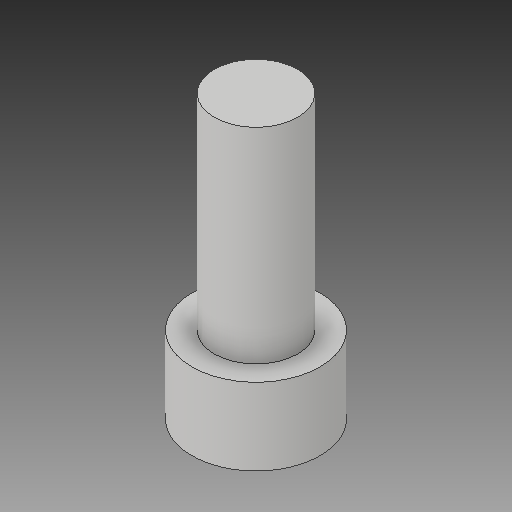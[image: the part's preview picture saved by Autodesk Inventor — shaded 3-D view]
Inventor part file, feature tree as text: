
AUTODESK INVENTOR PART (.ipt)
format: ipt  version: 2019 (Build 230136000, 136)  size: 97,792 bytes
history: native  units: mm
features: extrude x2, sketch x2
ambient origin geometry x8: Origin, YZ Plane, XZ Plane, XY Plane, X Axis, Y Axis, Z Axis, Center Point
bodies: Solid1 (feature_tree)
feature tree (4):
  extrude  "Extrusion1"  Depth=6.0mm TaperAngle=0.0deg
  extrude  "Extrusion2"  Depth=16.0mm TaperAngle=0.0deg
  sketch  "Sketch1"  dims[d0=10.0mm d1=6.0mm d2=0.0mm]
  sketch  "Sketch2"  dims[d3=6.5mm d4=16.0mm d5=0.0mm]
